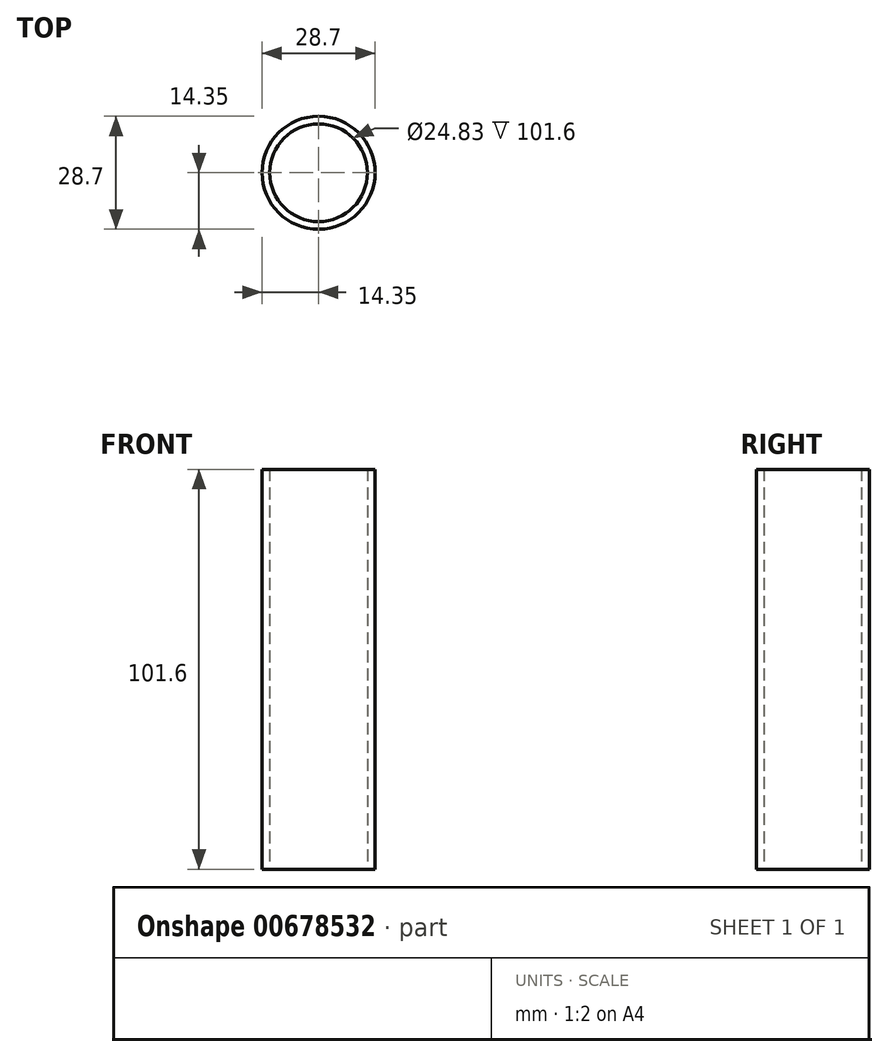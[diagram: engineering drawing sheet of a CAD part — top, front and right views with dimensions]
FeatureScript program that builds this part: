
annotation { "Feature Type Name" : "Feature", "Feature Type Description" : "" }
export const myFeature = defineFeature(function(context is Context, id is Id, definition is map)
    precondition{}
    {
        {
            var Q0;
            Q0=qCreatedBy(makeId("Top.planeOp"),FACE);
            var sketch = newSketch(context, id + "F0", { "sketchPlane" : qUnion([Q0])});
            skCircle(sketch, "E0", {"center": v(0, 0) * mm, "radius": 14.35 * mm});
            skCircle(sketch, "E1", {"center": v(0, 0) * mm, "radius": 12.41 * mm});
            skSolve(sketch);
        }
        {
            var Q0;
            Q0=makeQuery(id+"F0.imprint","IMPRINT",FACE,{"disambiguationData":[TD([[makeQuery(id+"F0.imprint","IMPRINT",EDGE,{"derivedFrom":sQuery(id+"F0.wireOp",EDGE,"E0")}),1.0]])]});
            extrude(context, id + "F1", {"entities" : qUnion([Q0]), "depth" : 101.6 * mm, "offsetDistance" : 25.4 * mm});
        }
    });
